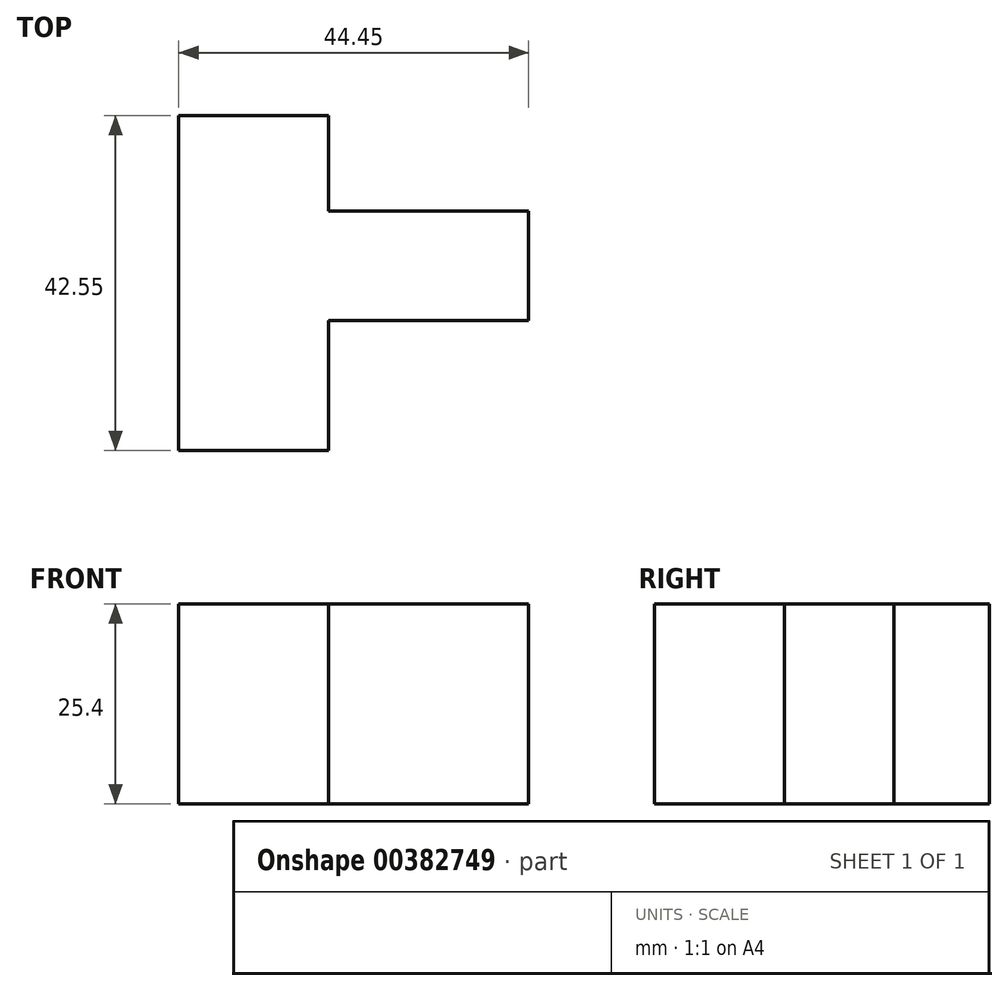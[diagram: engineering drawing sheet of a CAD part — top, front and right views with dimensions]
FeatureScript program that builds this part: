
annotation { "Feature Type Name" : "Feature", "Feature Type Description" : "" }
export const myFeature = defineFeature(function(context is Context, id is Id, definition is map)
    precondition{}
    {
        {
            var Q0;
            Q0=qCreatedBy(makeId("Top.planeOp"),FACE);
            var sketch = newSketch(context, id + "F0", { "sketchPlane" : qUnion([Q0])});
            skLineSegment(sketch, "E0", {"start": v(0, 26.05) * mm, "end": v(19.05, 26.05) * mm});
            skLineSegment(sketch, "E1", {"start": v(19.05, 26.05) * mm, "end": v(19.05, 13.9) * mm});
            skLineSegment(sketch, "E2", {"start": v(19.05, 13.9) * mm, "end": v(44.45, 13.9) * mm});
            skLineSegment(sketch, "E3", {"start": v(44.45, 13.9) * mm, "end": v(44.45, 0) * mm});
            skLineSegment(sketch, "E4", {"start": v(44.45, 0) * mm, "end": v(19.05, 0) * mm});
            skLineSegment(sketch, "E5", {"start": v(19.05, 0) * mm, "end": v(19.05, -16.5) * mm});
            skLineSegment(sketch, "E6", {"start": v(19.05, -16.5) * mm, "end": v(0, -16.5) * mm});
            skLineSegment(sketch, "E7", {"start": v(0, 26.05) * mm, "end": v(0, -16.5) * mm});
            skSolve(sketch);
        }
        {
            var Q0;
            Q0=makeQuery(id+"F0.imprint","IMPRINT",FACE,{"disambiguationData":[TD([[makeQuery(id+"F0.imprint","IMPRINT",EDGE,{"derivedFrom":sQuery(id+"F0.wireOp",EDGE,"E0")}),-1.0]])]});
            extrude(context, id + "F1", {"entities" : qUnion([Q0]), "depth" : 25.4 * mm});
        }
    });
